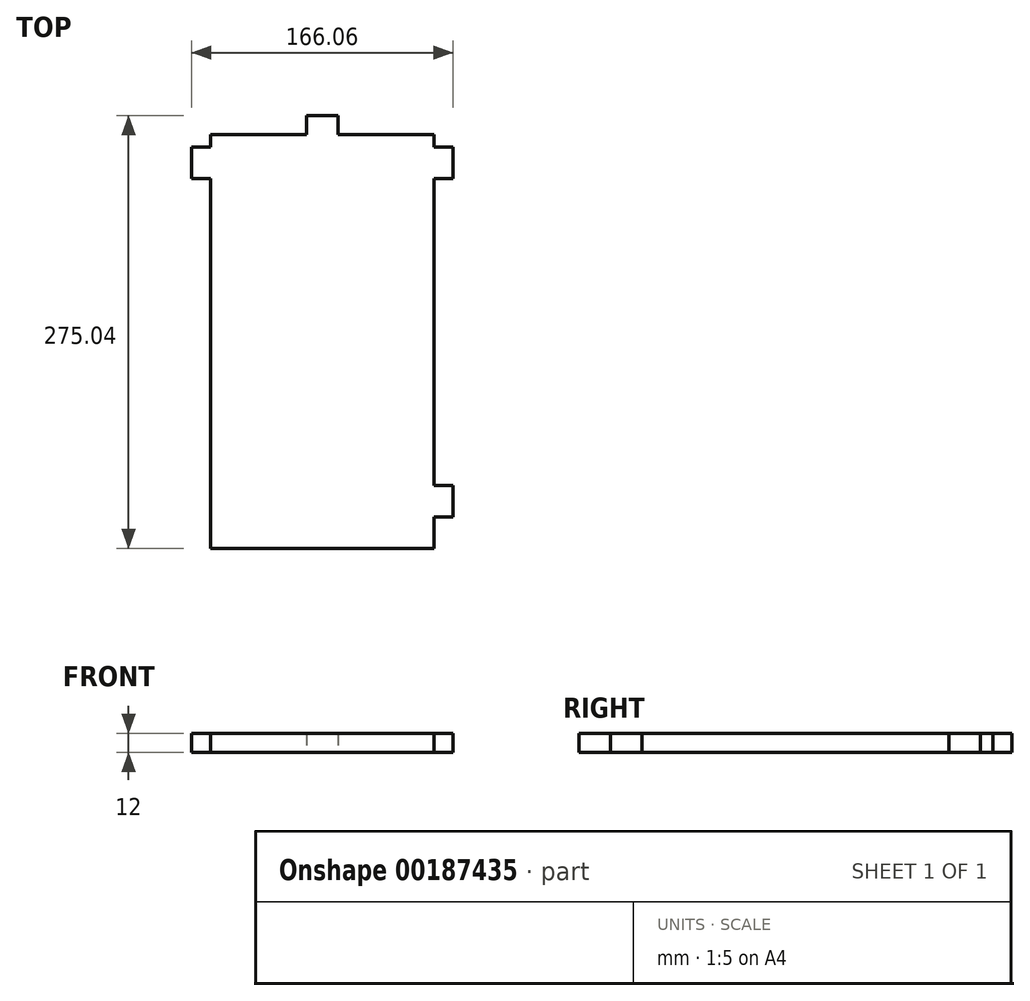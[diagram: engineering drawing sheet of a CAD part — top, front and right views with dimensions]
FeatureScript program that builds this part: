
annotation { "Feature Type Name" : "Feature", "Feature Type Description" : "" }
export const myFeature = defineFeature(function(context is Context, id is Id, definition is map)
    precondition{}
    {
        {
            var Q0;
            Q0=qCreatedBy(makeId("Top.planeOp"),FACE);
            var sketch = newSketch(context, id + "F0", { "sketchPlane" : qUnion([Q0])});
            skLineSegment(sketch, "E0.bottom", {"start": v(10, 137.52) * mm, "end": v(-10, 137.52) * mm});
            skLineSegment(sketch, "E0.top", {"start": v(71.03, -137.52) * mm, "end": v(-71.03, -137.52) * mm});
            skLineSegment(sketch, "E0.left", {"start": v(71.03, 125.52) * mm, "end": v(71.02, -137.52) * mm});
            skLineSegment(sketch, "E0.right", {"start": v(-71.02, 125.52) * mm, "end": v(-71.03, -137.52) * mm});
            skPoint(sketch, "E0.middle", {"position": v(0, 0) * mm});
            skLineSegment(sketch, "E1.bottom", {"start": v(-71.03, 117.52) * mm, "end": v(-83.03, 117.52) * mm});
            skLineSegment(sketch, "E1.top", {"start": v(-71.03, 97.52) * mm, "end": v(-83.03, 97.52) * mm});
            skLineSegment(sketch, "E1.left", {"start": v(-71.02, 117.52) * mm, "end": v(-71.02, 97.52) * mm});
            skLineSegment(sketch, "E1.right", {"start": v(-83.02, 117.52) * mm, "end": v(-83.02, 97.52) * mm});
            skLineSegment(sketch, "E2.MirrorCS", {"start": v(-71.02, -117.52) * mm, "end": v(-71.02, -97.52) * mm});
            skLineSegment(sketch, "E3.MirrorCS", {"start": v(-83.02, -117.52) * mm, "end": v(-83.02, -97.52) * mm});
            skLineSegment(sketch, "E4.MirrorCS", {"start": v(-71.03, -117.52) * mm, "end": v(-83.03, -117.52) * mm});
            skLineSegment(sketch, "E5.MirrorCS", {"start": v(-71.03, -97.52) * mm, "end": v(-83.03, -97.52) * mm});
            skLineSegment(sketch, "E6.MirrorCS", {"start": v(71.03, 117.52) * mm, "end": v(83.03, 117.52) * mm});
            skLineSegment(sketch, "E7.MirrorCS", {"start": v(71.03, -97.52) * mm, "end": v(83.03, -97.52) * mm});
            skLineSegment(sketch, "E8.MirrorCS", {"start": v(71.03, 97.52) * mm, "end": v(83.03, 97.52) * mm});
            skLineSegment(sketch, "E9.MirrorCS", {"start": v(71.03, -117.52) * mm, "end": v(83.03, -117.52) * mm});
            skLineSegment(sketch, "E10.MirrorCS", {"start": v(71.02, -117.52) * mm, "end": v(71.02, -97.52) * mm});
            skLineSegment(sketch, "E11.MirrorCS", {"start": v(83.02, 117.52) * mm, "end": v(83.02, 97.52) * mm});
            skLineSegment(sketch, "E12.MirrorCS", {"start": v(83.02, -117.52) * mm, "end": v(83.02, -97.52) * mm});
            skLineSegment(sketch, "E13.MirrorCS", {"start": v(71.02, 117.52) * mm, "end": v(71.02, 97.52) * mm});
            skPoint(sketch, "E14.endSnap0", {"position": v(0, 137.52) * mm});
            skLineSegment(sketch, "E15.right", {"start": v(-10, 127.52) * mm, "end": v(-10, 137.52) * mm});
            skPoint(sketch, "E15.top.end.orphan", {"position": v(-10, 147.52) * mm});
            skPoint(sketch, "E16.orphan", {"position": v(10, 147.52) * mm});
            skLineSegment(sketch, "E17.top", {"start": v(-10, 137.52) * mm, "end": v(10, 137.52) * mm});
            skLineSegment(sketch, "E17.right", {"start": v(10, 127.52) * mm, "end": v(10, 137.52) * mm});
            skPoint(sketch, "E14.end.orphan", {"position": v(0, 125.21) * mm});
            skLineSegment(sketch, "E18", {"start": v(-71.03, 125.52) * mm, "end": v(71.03, 125.52) * mm});
            skLineSegment(sketch, "E19", {"start": v(-10, 127.52) * mm, "end": v(-10, 125.52) * mm});
            skLineSegment(sketch, "E20", {"start": v(10, 127.52) * mm, "end": v(10, 125.52) * mm});
            skPoint(sketch, "E21.orphan", {"position": v(71.03, 137.52) * mm});
            skPoint(sketch, "E22.orphan", {"position": v(-71.03, 137.52) * mm});
            skSolve(sketch);
        }
        {
            var Q0;
            Q0=makeQuery(id+"F0.imprint","IMPRINT",FACE,{"disambiguationData":[TD([[makeQuery(id+"F0.imprint","IMPRINT",EDGE,{"derivedFrom":sQuery(id+"F0.wireOp",EDGE,"E1.bottom")}),1.0]])]});
            var Q1;
            {var subQ2=sQuery(id+"F0.wireOp",EDGE,"E0.top");Q1=makeQuery(id+"F0.imprint","IMPRINT",FACE,{"disambiguationData":[TD([[makeQuery(id+"F0.imprint","IMPRINT",EDGE,{"derivedFrom":subQ2}),-1.0]])]});}
            var Q2;
            {var subQ0=sQuery(id+"F0.wireOp",EDGE,"E14");var subQ1=sQuery(id+"F0.wireOp",EDGE,"E0.bottom");var subQ2=makeQuery(id+"F0.imprint","INTERSECT",VERTEX,{"derivedFrom":[subQ1,subQ0]});Q2=makeQuery(id+"F0.imprint","IMPRINT",FACE,{"disambiguationData":[TD([[makeQuery(id+"F0.imprint","IMPRINT",EDGE,{"disambiguationData":[TD([[subQ2,-1.0]])],"derivedFrom":subQ1}),1.0]])]});}
            var Q3;
            {var subQ0=sQuery(id+"F0.wireOp",EDGE,"E14");var subQ1=sQuery(id+"F0.wireOp",EDGE,"E0.bottom");var subQ2=makeQuery(id+"F0.imprint","INTERSECT",VERTEX,{"derivedFrom":[subQ1,subQ0]});Q3=makeQuery(id+"F0.imprint","IMPRINT",FACE,{"disambiguationData":[TD([[makeQuery(id+"F0.imprint","IMPRINT",EDGE,{"disambiguationData":[TD([[subQ2,1.0]])],"derivedFrom":subQ1}),1.0]])]});}
            var Q4;
            Q4=makeQuery(id+"F0.imprint","IMPRINT",FACE,{"disambiguationData":[TD([[makeQuery(id+"F0.imprint","IMPRINT",EDGE,{"derivedFrom":sQuery(id+"F0.wireOp",EDGE,"E6.MirrorCS")}),-1.0]])]});
            var Q5;
            Q5=makeQuery(id+"F0.imprint","IMPRINT",FACE,{"disambiguationData":[TD([[makeQuery(id+"F0.imprint","IMPRINT",EDGE,{"derivedFrom":sQuery(id+"F0.wireOp",EDGE,"E2.MirrorCS")}),1.0]])]});
            var Q6;
            Q6=makeQuery(id+"F0.imprint","IMPRINT",FACE,{"disambiguationData":[TD([[makeQuery(id+"F0.imprint","IMPRINT",EDGE,{"derivedFrom":sQuery(id+"F0.wireOp",EDGE,"E7.MirrorCS")}),-1.0]])]});
            var Q7;
            Q7=makeQuery(id+"F0.imprint","IMPRINT",FACE,{"disambiguationData":[TD([[makeQuery(id+"F0.imprint","IMPRINT",EDGE,{"derivedFrom":sQuery(id+"F0.wireOp",EDGE,"E17.top")}),-1.0]])]});
            extrude(context, id + "F1", {"entities" : qUnion([Q0, Q1, Q2, Q3, Q4, Q5, Q6, Q7]), "offsetDistance" : 25 * mm, "depth" : 12 * mm});
        }
    });
